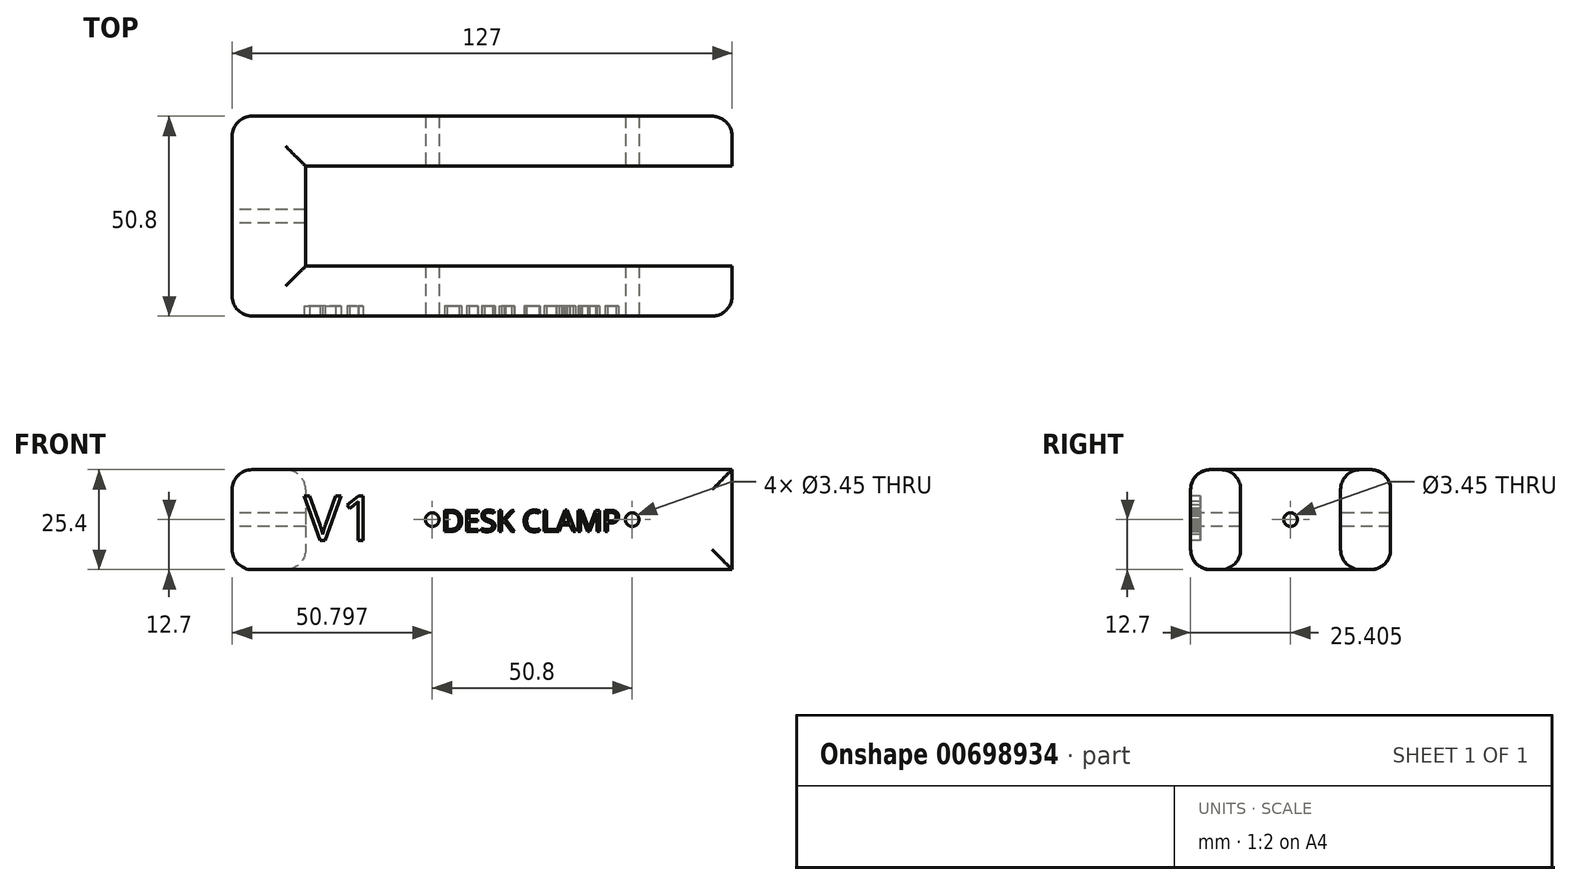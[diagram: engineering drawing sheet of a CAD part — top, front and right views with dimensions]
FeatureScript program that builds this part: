
annotation { "Feature Type Name" : "Feature", "Feature Type Description" : "" }
export const myFeature = defineFeature(function(context is Context, id is Id, definition is map)
    precondition{}
    {
        {
            var Q0;
            Q0=qCreatedBy(makeId("Top.planeOp"),FACE);
            var sketch = newSketch(context, id + "F0", { "sketchPlane" : qUnion([Q0])});
            skLineSegment(sketch, "E0", {"start": v(-20.42, -8.74) * mm, "end": v(-20.42, 16.66) * mm});
            skLineSegment(sketch, "E1", {"start": v(-20.42, 16.66) * mm, "end": v(87.95, 16.66) * mm});
            skLineSegment(sketch, "E2", {"start": v(87.95, 16.66) * mm, "end": v(87.95, 29.36) * mm});
            skLineSegment(sketch, "E3", {"start": v(87.95, 29.36) * mm, "end": v(-39.05, 29.36) * mm});
            skLineSegment(sketch, "E4", {"start": v(-39.05, 29.36) * mm, "end": v(-39.05, -21.44) * mm});
            skLineSegment(sketch, "E5", {"start": v(-39.05, -21.44) * mm, "end": v(87.95, -21.44) * mm});
            skLineSegment(sketch, "E6", {"start": v(87.95, -21.44) * mm, "end": v(87.95, -8.74) * mm});
            skLineSegment(sketch, "E7", {"start": v(87.95, -8.74) * mm, "end": v(-20.42, -8.74) * mm});
            skSolve(sketch);
        }
        {
            var Q0;
            Q0 = qSketchRegion(id + "F0", true);
            extrude(context, id + "F1", {"entities" : qUnion([Q0]), "depth" : 25.4 * mm, "offsetDistance" : 25.4 * mm});
        }
        {
            var Q0;
            Q0=makeQuery(id+"F1.opExtrude","SWEPT_FACE",FACE,{"disambiguationData":[OSD([sQuery(id+"F0.wireOp",EDGE,"E5")])]});
            var sketch = newSketch(context, id + "F2", { "sketchPlane" : qUnion([Q0])});
            skPoint(sketch, "E8", {"position": v(62.55, 12.7) * mm});
            skPoint(sketch, "E9", {"position": v(11.75, 12.7) * mm});
            skSolve(sketch);
        }
        {
            var Q0;
            Q0=sQuery(id+"F2.wireOp",VERTEX,"E8");
            var Q1;
            Q1=makeQuery(id+"F1.opExtrude","SWEPT_BODY",BODY,{"disambiguationData":[OSD([sQuery(id+"F0.wireOp",EDGE,"E0"),sQuery(id+"F0.wireOp",EDGE,"E1"),sQuery(id+"F0.wireOp",EDGE,"E2"),sQuery(id+"F0.wireOp",EDGE,"E3"),sQuery(id+"F0.wireOp",EDGE,"E4"),sQuery(id+"F0.wireOp",EDGE,"E5"),sQuery(id+"F0.wireOp",EDGE,"E6"),sQuery(id+"F0.wireOp",EDGE,"E7")])]});
            hole(context, id + "F3", {"style" : HoleStyle.SIMPLE, "endStyle" : HoleEndStyle.THROUGH, "standardTappedOrClearance" : lookupTablePath({ "standard" : "ANSI", "engagement" : "75%", "pitch" : "32 tpi", "size" : "#8", "type" : "Tapped" }), "standardBlindInLast" : lookupTablePath({ "standard" : "ANSI", "engagement" : "75%", "pitch" : "32 tpi", "size" : "#8", "type" : "Tapped" }), "holeDiameter" : 3.45 * mm, "majorDiameter" : 4.17 * mm, "showTappedDepth" : true, "isTappedThrough" : true, "tappedDepth" : 3.97 * mm, "tapClearance" : 3, "locations" : qUnion([Q0]), "scope" : qUnion([Q1])});
        }
        {
            var Q0;
            Q0=makeQuery(id+"F1.opExtrude","SWEPT_FACE",FACE,{"disambiguationData":[OSD([sQuery(id+"F0.wireOp",EDGE,"E4")])]});
            var sketch = newSketch(context, id + "F4", { "sketchPlane" : qUnion([Q0])});
            skPoint(sketch, "E10", {"position": v(-3.96, 12.7) * mm});
            skLineSegment(sketch, "E11", {"start": v(-29.36, 25.4) * mm, "end": v(21.44, 0) * mm, "construction": true});
            skLineSegment(sketch, "E12", {"start": v(21.44, 0) * mm, "end": v(21.44, 25.4) * mm, "construction": true});
            skLineSegment(sketch, "E13", {"start": v(21.44, 25.4) * mm, "end": v(-29.36, 0) * mm, "construction": true});
            skSolve(sketch);
        }
        {
            var Q0;
            Q0=sQuery(id+"F4.wireOp",VERTEX,"E10");
            var Q1;
            Q1=makeQuery(id+"F1.opExtrude","SWEPT_BODY",BODY,{"disambiguationData":[OSD([sQuery(id+"F0.wireOp",EDGE,"E0"),sQuery(id+"F0.wireOp",EDGE,"E1"),sQuery(id+"F0.wireOp",EDGE,"E2"),sQuery(id+"F0.wireOp",EDGE,"E3"),sQuery(id+"F0.wireOp",EDGE,"E4"),sQuery(id+"F0.wireOp",EDGE,"E5"),sQuery(id+"F0.wireOp",EDGE,"E6"),sQuery(id+"F0.wireOp",EDGE,"E7")])]});
            hole(context, id + "F5", {"style" : HoleStyle.SIMPLE, "endStyle" : HoleEndStyle.THROUGH, "standardTappedOrClearance" : lookupTablePath({ "standard" : "ANSI", "engagement" : "75%", "pitch" : "32 tpi", "size" : "#8", "type" : "Tapped" }), "standardBlindInLast" : lookupTablePath({ "standard" : "ANSI", "engagement" : "75%", "pitch" : "32 tpi", "size" : "#8", "type" : "Tapped" }), "holeDiameter" : 3.45 * mm, "majorDiameter" : 4.17 * mm, "showTappedDepth" : true, "isTappedThrough" : true, "tappedDepth" : 3.96 * mm, "tapClearance" : 3, "locations" : qUnion([Q0]), "scope" : qUnion([Q1])});
        }
        {
            var Q0;
            Q0=sQuery(id+"F2.wireOp",VERTEX,"E9");
            var Q1;
            Q1=makeQuery(id+"F1.opExtrude","SWEPT_BODY",BODY,{"disambiguationData":[OSD([sQuery(id+"F0.wireOp",EDGE,"E0"),sQuery(id+"F0.wireOp",EDGE,"E1"),sQuery(id+"F0.wireOp",EDGE,"E2"),sQuery(id+"F0.wireOp",EDGE,"E3"),sQuery(id+"F0.wireOp",EDGE,"E4"),sQuery(id+"F0.wireOp",EDGE,"E5"),sQuery(id+"F0.wireOp",EDGE,"E6"),sQuery(id+"F0.wireOp",EDGE,"E7")])]});
            hole(context, id + "F6", {"style" : HoleStyle.SIMPLE, "endStyle" : HoleEndStyle.THROUGH, "standardTappedOrClearance" : lookupTablePath({ "standard" : "ANSI", "engagement" : "75%", "pitch" : "32 tpi", "size" : "#8", "type" : "Tapped" }), "standardBlindInLast" : lookupTablePath({ "standard" : "ANSI", "engagement" : "75%", "pitch" : "32 tpi", "size" : "#8", "type" : "Tapped" }), "holeDiameter" : 3.45 * mm, "majorDiameter" : 4.17 * mm, "showTappedDepth" : true, "isTappedThrough" : true, "tappedDepth" : 3.96 * mm, "tapClearance" : 3, "locations" : qUnion([Q0]), "scope" : qUnion([Q1])});
        }
        {
            var Q0;
            {var subQ0=sQuery(id+"F0.wireOp",EDGE,"E5");Q0=makeQuery(id+"F2.imprint","IMPRINT",FACE,{"disambiguationData":[TD([[makeQuery(id+"F2.imprint","IMPRINT",EDGE,{"derivedFrom":makeQuery(id+"F1.opExtrude","CAP_EDGE",EDGE,{"disambiguationData":[OSD([subQ0])],"isStart":true})}),1.0]])]});}
            var sketch = newSketch(context, id + "F7", { "sketchPlane" : qUnion([Q0])});
            skText(sketch, "E14", { "text": "DESK CLAMP", "fontName": "OpenSans-Regular.ttf"});
            skText(sketch, "E15", { "text": "V1", "fontName": "OpenSans-Regular.ttf"});
            const initialGuessF7  = {"E14": [0.01419, 0.00968, 1, 0, 0.00544], "E15": [-0.02075, 0.00742, 1, 0, 0.01135]};
            skSetInitialGuess(sketch, initialGuessF7);
            skSolve(sketch);
        }
        {
            var Q0;
            Q0 = qSketchRegion(id + "F7", true);
            extrude(context, id + "F8", {"entities" : qUnion([Q0]), "operationType" : NewBodyOperationType.REMOVE, "oppositeDirection" : true, "depth" : 2.54 * mm, "offsetDistance" : 25.4 * mm});
        }
        {
            var Q0;
            Q0=makeQuery(id+"F1.opExtrude","CAP_EDGE",EDGE,{"disambiguationData":[OSD([sQuery(id+"F0.wireOp",EDGE,"E7")])],"isStart":false});
            var Q1;
            Q1=makeQuery(id+"F1.opExtrude","CAP_EDGE",EDGE,{"disambiguationData":[OSD([sQuery(id+"F0.wireOp",EDGE,"E0")])],"isStart":false});
            var Q2;
            Q2=makeQuery(id+"F1.opExtrude","CAP_EDGE",EDGE,{"disambiguationData":[OSD([sQuery(id+"F0.wireOp",EDGE,"E1")])],"isStart":false});
            var Q3;
            Q3=makeQuery(id+"F1.opExtrude","CAP_EDGE",EDGE,{"disambiguationData":[OSD([sQuery(id+"F0.wireOp",EDGE,"E3")])],"isStart":false});
            var Q4;
            Q4=makeQuery(id+"F1.opExtrude","CAP_EDGE",EDGE,{"disambiguationData":[OSD([sQuery(id+"F0.wireOp",EDGE,"E4")])],"isStart":false});
            var Q5;
            Q5=makeQuery(id+"F1.opExtrude","CAP_EDGE",EDGE,{"disambiguationData":[OSD([sQuery(id+"F0.wireOp",EDGE,"E5")])],"isStart":true});
            var Q6;
            Q6=makeQuery(id+"F1.opExtrude","CAP_EDGE",EDGE,{"disambiguationData":[OSD([sQuery(id+"F0.wireOp",EDGE,"E3")])],"isStart":true});
            var Q7;
            Q7=makeQuery(id+"F1.opExtrude","CAP_EDGE",EDGE,{"disambiguationData":[OSD([sQuery(id+"F0.wireOp",EDGE,"E4")])],"isStart":true});
            var Q8;
            Q8=makeQuery(id+"F1.opExtrude","CAP_EDGE",EDGE,{"disambiguationData":[OSD([sQuery(id+"F0.wireOp",EDGE,"E5")])],"isStart":false});
            var Q9;
            Q9=makeQuery(id+"F1.opExtrude","SWEPT_EDGE",EDGE,{"disambiguationData":[OSD([sQuery(id+"F0.wireOp",EDGE,"E5"),sQuery(id+"F0.wireOp",EDGE,"E6")])]});
            var Q10;
            Q10=makeQuery(id+"F1.opExtrude","SWEPT_EDGE",EDGE,{"disambiguationData":[OSD([sQuery(id+"F0.wireOp",EDGE,"E3"),sQuery(id+"F0.wireOp",EDGE,"E4")])]});
            var Q11;
            Q11=makeQuery(id+"F1.opExtrude","SWEPT_EDGE",EDGE,{"disambiguationData":[OSD([sQuery(id+"F0.wireOp",EDGE,"E4"),sQuery(id+"F0.wireOp",EDGE,"E5")])]});
            var Q12;
            Q12=makeQuery(id+"F1.opExtrude","CAP_EDGE",EDGE,{"disambiguationData":[OSD([sQuery(id+"F0.wireOp",EDGE,"E1")])],"isStart":true});
            var Q13;
            Q13=makeQuery(id+"F1.opExtrude","CAP_EDGE",EDGE,{"disambiguationData":[OSD([sQuery(id+"F0.wireOp",EDGE,"E0")])],"isStart":true});
            var Q14;
            Q14=makeQuery(id+"F1.opExtrude","CAP_EDGE",EDGE,{"disambiguationData":[OSD([sQuery(id+"F0.wireOp",EDGE,"E7")])],"isStart":true});
            var Q15;
            Q15=makeQuery(id+"F1.opExtrude","SWEPT_EDGE",EDGE,{"disambiguationData":[OSD([sQuery(id+"F0.wireOp",EDGE,"E2"),sQuery(id+"F0.wireOp",EDGE,"E3")])]});
            fillet(context, id + "F9", {"entities" : qUnion([Q0, Q1, Q2, Q3, Q4, Q5, Q6, Q7, Q8, Q9, Q10, Q11, Q12, Q13, Q14, Q15]), "radius" : 5.08 * mm, "tangentPropagation" : true, "allowEdgeOverflow" : false});
        }
    });
